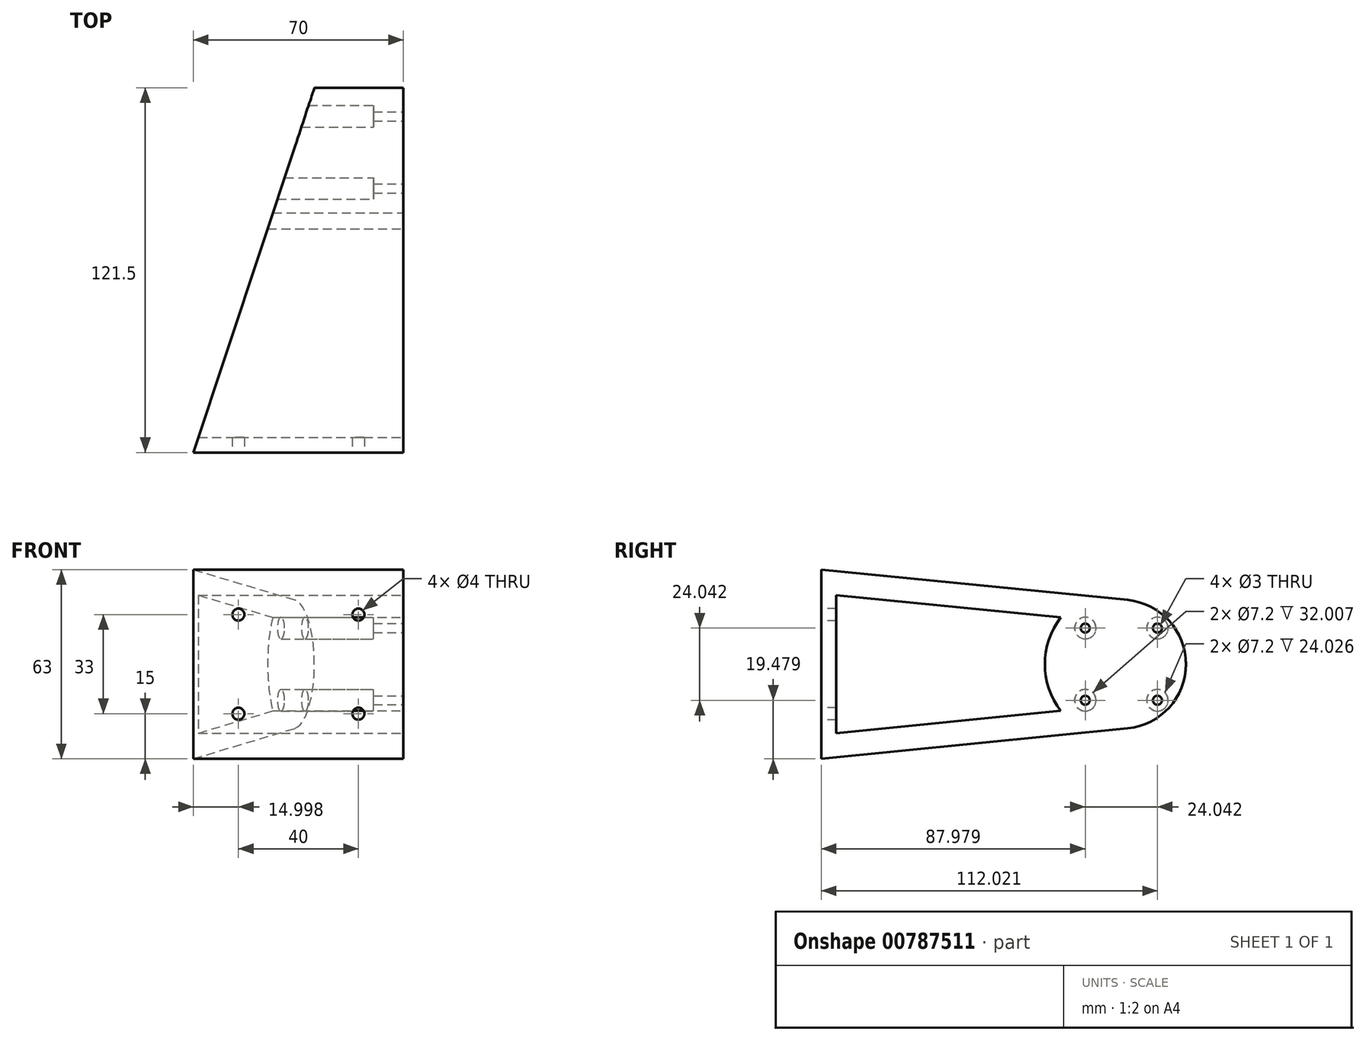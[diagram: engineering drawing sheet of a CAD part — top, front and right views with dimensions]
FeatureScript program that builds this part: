
annotation { "Feature Type Name" : "Feature", "Feature Type Description" : "" }
export const myFeature = defineFeature(function(context is Context, id is Id, definition is map)
    precondition{}
    {
        {
            var Q0;
            Q0=qCreatedBy(makeId("Top.planeOp"),FACE);
            var sketch = newSketch(context, id + "F0", { "sketchPlane" : qUnion([Q0])});
            skLineSegment(sketch, "E0", {"start": v(17.03, 72.23) * mm, "end": v(-12.97, 72.23) * mm});
            skLineSegment(sketch, "E1", {"start": v(-12.97, 72.23) * mm, "end": v(-52.97, -48.27) * mm});
            skLineSegment(sketch, "E2", {"start": v(-52.97, -48.27) * mm, "end": v(17.03, -48.27) * mm});
            skLineSegment(sketch, "E3", {"start": v(17.03, -48.27) * mm, "end": v(17.03, 72.23) * mm});
            skSolve(sketch);
        }
        {
            var Q0;
            Q0=makeQuery(id+"F0.imprint","IMPRINT",FACE,{"disambiguationData":[TD([[makeQuery(id+"F0.imprint","IMPRINT",EDGE,{"derivedFrom":sQuery(id+"F0.wireOp",EDGE,"E0")}),1.0]])]});
            extrude(context, id + "F1", {"entities" : qUnion([Q0]), "depth" : 43 * mm, "offsetDistance" : 25.4 * mm});
        }
        {
            var Q0;
            Q0=makeQuery(id+"F1.opExtrude","SWEPT_FACE",FACE,{"disambiguationData":[OSD([sQuery(id+"F0.wireOp",EDGE,"E3")])]});
            var sketch = newSketch(context, id + "F2", { "sketchPlane" : qUnion([Q0])});
            skLineSegment(sketch, "E4.bottom", {"start": v(72.23, 43) * mm, "end": v(51.73, 43) * mm});
            skLineSegment(sketch, "E4.top", {"start": v(72.23, 0) * mm, "end": v(51.73, 0) * mm});
            skLineSegment(sketch, "E4.left", {"start": v(72.23, 43) * mm, "end": v(72.23, 0) * mm});
            skLineSegment(sketch, "E4.right", {"start": v(51.73, 43) * mm, "end": v(51.73, 0) * mm, "construction": true});
            skCircle(sketch, "E5", {"center": v(51.73, 21.5) * mm, "radius": 21.5 * mm});
            skCircle(sketch, "E6", {"center": v(51.73, 21.5) * mm, "radius": 17 * mm, "construction": true});
            skCircle(sketch, "E7", {"center": v(51.73, 4.5) * mm, "radius": 1.5 * mm, "construction": true});
            skCircle(sketch, "E8.1.0", {"center": v(63.75, 9.48) * mm, "radius": 1.5 * mm});
            skCircle(sketch, "E8.2.0", {"center": v(68.73, 21.5) * mm, "radius": 1.5 * mm, "construction": true});
            skCircle(sketch, "E8.3.0", {"center": v(63.75, 33.52) * mm, "radius": 1.5 * mm});
            skCircle(sketch, "E8.4.0", {"center": v(51.73, 38.5) * mm, "radius": 1.5 * mm, "construction": true});
            skCircle(sketch, "E8.5.0", {"center": v(39.7, 33.52) * mm, "radius": 1.5 * mm});
            skCircle(sketch, "E8.6.0", {"center": v(34.73, 21.5) * mm, "radius": 1.5 * mm, "construction": true});
            skCircle(sketch, "E8.7.0", {"center": v(39.7, 9.48) * mm, "radius": 1.5 * mm});
            skLineSegment(sketch, "E9", {"start": v(-48.27, 43) * mm, "end": v(-48.27, 53) * mm});
            skLineSegment(sketch, "E10", {"start": v(-48.27, 53) * mm, "end": v(53.85, 42.9) * mm});
            skLineSegment(sketch, "E11", {"start": v(-48.27, 0) * mm, "end": v(-48.27, -10) * mm});
            skLineSegment(sketch, "E12", {"start": v(-48.27, -10) * mm, "end": v(53.85, 0.1) * mm});
            skCircle(sketch, "E13", {"center": v(51.73, 21.5) * mm, "radius": 25.5 * mm});
            skLineSegment(sketch, "E14.0", {"start": v(-48.96, -2.03) * mm, "end": v(54.65, 8.22) * mm});
            skLineSegment(sketch, "E15.0", {"start": v(-49, 45.03) * mm, "end": v(54.6, 34.78) * mm});
            skLineSegment(sketch, "E16.0", {"start": v(-43.27, 44.47) * mm, "end": v(-43.27, -1.47) * mm});
            skCircle(sketch, "E17", {"center": v(63.75, 33.52) * mm, "radius": 3.6 * mm});
            skCircle(sketch, "E18", {"center": v(63.75, 9.48) * mm, "radius": 3.6 * mm});
            skCircle(sketch, "E19", {"center": v(39.7, 33.52) * mm, "radius": 3.6 * mm});
            skCircle(sketch, "E20", {"center": v(39.7, 9.48) * mm, "radius": 3.6 * mm});
            skSolve(sketch);
        }
        {
            var Q0;
            Q0=makeQuery(id+"F2.imprint","IMPRINT",FACE,{"disambiguationData":[TD([[makeQuery(id+"F2.imprint","IMPRINT",EDGE,{"derivedFrom":sQuery(id+"F2.wireOp",EDGE,"E8.1.0")}),1.0]])]});
            var Q1;
            Q1=makeQuery(id+"F2.imprint","IMPRINT",FACE,{"disambiguationData":[TD([[makeQuery(id+"F2.imprint","IMPRINT",EDGE,{"derivedFrom":sQuery(id+"F2.wireOp",EDGE,"E8.3.0")}),1.0]])]});
            var Q2;
            Q2=makeQuery(id+"F2.imprint","IMPRINT",FACE,{"disambiguationData":[TD([[makeQuery(id+"F2.imprint","IMPRINT",EDGE,{"derivedFrom":sQuery(id+"F2.wireOp",EDGE,"E8.5.0")}),1.0]])]});
            var Q3;
            Q3=makeQuery(id+"F2.imprint","IMPRINT",FACE,{"disambiguationData":[TD([[makeQuery(id+"F2.imprint","IMPRINT",EDGE,{"derivedFrom":sQuery(id+"F2.wireOp",EDGE,"E8.7.0")}),1.0]])]});
            var Q4;
            {var subQ0=sQuery(id+"F2.wireOp",EDGE,"E4.left");var subQ1=sQuery(id+"F2.wireOp",EDGE,"E4.bottom");var subQ2=makeQuery(id+"F2.imprint","INTERSECT",VERTEX,{"derivedFrom":[subQ1,subQ0]});Q4=makeQuery(id+"F2.imprint","IMPRINT",FACE,{"disambiguationData":[TD([[makeQuery(id+"F2.imprint","IMPRINT",EDGE,{"disambiguationData":[TD([[subQ2,1.0]])],"derivedFrom":subQ1}),-1.0]])]});}
            var Q5;
            {var subQ0=sQuery(id+"F2.wireOp",EDGE,"E4.left");var subQ1=sQuery(id+"F2.wireOp",EDGE,"E4.top");var subQ2=makeQuery(id+"F2.imprint","INTERSECT",VERTEX,{"derivedFrom":[subQ1,subQ0]});Q5=makeQuery(id+"F2.imprint","IMPRINT",FACE,{"disambiguationData":[TD([[makeQuery(id+"F2.imprint","IMPRINT",EDGE,{"disambiguationData":[TD([[subQ2,1.0]])],"derivedFrom":subQ1}),1.0]])]});}
            var Q6;
            {var subQ0=sQuery(id+"F2.wireOp",EDGE,"E15.0");var subQ1=sQuery(id+"F2.wireOp",EDGE,"E13");var subQ2=makeQuery(id+"F2.imprint","INTERSECT",VERTEX,{"derivedFrom":[subQ1,subQ0]});Q6=makeQuery(id+"F2.imprint","IMPRINT",FACE,{"disambiguationData":[TD([[makeQuery(id+"F2.imprint","IMPRINT",EDGE,{"disambiguationData":[TD([[subQ2,-1.0]])],"derivedFrom":subQ1}),-1.0]])]});}
            var Q7;
            {var subQ5=sQuery(id+"F2.wireOp",EDGE,"E4.bottom");var subQ7=sQuery(id+"F2.wireOp",EDGE,"E13");var subQ9=makeQuery(id+"F2.imprint","INTERSECT",VERTEX,{"derivedFrom":[subQ5,subQ7]});Q7=makeQuery(id+"F2.imprint","IMPRINT",FACE,{"disambiguationData":[TD([[makeQuery(id+"F2.imprint","IMPRINT",EDGE,{"disambiguationData":[TD([[subQ9,1.0]])],"derivedFrom":subQ5}),-1.0]])]});}
            var Q8;
            {var subQ3=sQuery(id+"F2.wireOp",EDGE,"E4.top");var subQ7=sQuery(id+"F2.wireOp",EDGE,"E13");var subQ9=makeQuery(id+"F2.imprint","INTERSECT",VERTEX,{"derivedFrom":[subQ3,subQ7]});Q8=makeQuery(id+"F2.imprint","IMPRINT",FACE,{"disambiguationData":[TD([[makeQuery(id+"F2.imprint","IMPRINT",EDGE,{"disambiguationData":[TD([[subQ9,1.0]])],"derivedFrom":subQ3}),1.0]])]});}
            extrude(context, id + "F3", {"entities" : qUnion([Q0, Q1, Q2, Q3, Q4, Q5, Q6, Q7, Q8]), "operationType" : NewBodyOperationType.REMOVE, "oppositeDirection" : true, "depth" : 76.2 * mm, "offsetDistance" : 25.4 * mm});
        }
        {
            var Q0;
            {var subQ4=sQuery(id+"F2.wireOp",EDGE,"E14.0");var subQ6=sQuery(id+"F2.wireOp",EDGE,"E16.0");var subQ8=makeQuery(id+"F2.imprint","INTERSECT",VERTEX,{"derivedFrom":[subQ4,subQ6]});Q0=makeQuery(id+"F2.imprint","IMPRINT",FACE,{"disambiguationData":[TD([[makeQuery(id+"F2.imprint","IMPRINT",EDGE,{"disambiguationData":[TD([[subQ8,1.0]])],"derivedFrom":subQ4}),1.0]])]});}
            var Q1;
            {var subQ1=sQuery(id+"F2.wireOp",EDGE,"E12");var subQ5=sQuery(id+"F2.wireOp",EDGE,"E11");var subQ6=makeQuery(id+"F2.imprint","INTERSECT",VERTEX,{"derivedFrom":[subQ5,subQ1]});Q1=makeQuery(id+"F2.imprint","IMPRINT",FACE,{"disambiguationData":[TD([[makeQuery(id+"F2.imprint","IMPRINT",EDGE,{"disambiguationData":[TD([[subQ6,1.0]])],"derivedFrom":subQ5}),1.0]])]});}
            var Q2;
            {var subQ4=sQuery(id+"F2.wireOp",EDGE,"E15.0");var subQ6=sQuery(id+"F2.wireOp",EDGE,"E16.0");var subQ7=makeQuery(id+"F2.imprint","INTERSECT",VERTEX,{"derivedFrom":[subQ4,subQ6]});Q2=makeQuery(id+"F2.imprint","IMPRINT",FACE,{"disambiguationData":[TD([[makeQuery(id+"F2.imprint","IMPRINT",EDGE,{"disambiguationData":[TD([[subQ7,1.0]])],"derivedFrom":subQ4}),-1.0]])]});}
            var Q3;
            {var subQ1=sQuery(id+"F2.wireOp",EDGE,"E10");var subQ7=sQuery(id+"F2.wireOp",EDGE,"E9");var subQ9=makeQuery(id+"F2.imprint","INTERSECT",VERTEX,{"derivedFrom":[subQ7,subQ1]});Q3=makeQuery(id+"F2.imprint","IMPRINT",FACE,{"disambiguationData":[TD([[makeQuery(id+"F2.imprint","IMPRINT",EDGE,{"disambiguationData":[TD([[subQ9,1.0]])],"derivedFrom":subQ7}),-1.0]])]});}
            var Q4;
            {var subQ3=sQuery(id+"F2.wireOp",EDGE,"E10");var subQ5=sQuery(id+"F2.wireOp",EDGE,"E13");var subQ6=makeQuery(id+"F2.imprint","INTERSECT",VERTEX,{"derivedFrom":[subQ3,subQ5]});Q4=makeQuery(id+"F2.imprint","IMPRINT",FACE,{"disambiguationData":[TD([[makeQuery(id+"F2.imprint","IMPRINT",EDGE,{"disambiguationData":[TD([[subQ6,-1.0]])],"derivedFrom":subQ3}),-1.0]])]});}
            var Q5;
            {var subQ3=sQuery(id+"F2.wireOp",EDGE,"E12");var subQ5=sQuery(id+"F2.wireOp",EDGE,"E13");var subQ6=makeQuery(id+"F2.imprint","INTERSECT",VERTEX,{"derivedFrom":[subQ3,subQ5]});Q5=makeQuery(id+"F2.imprint","IMPRINT",FACE,{"disambiguationData":[TD([[makeQuery(id+"F2.imprint","IMPRINT",EDGE,{"disambiguationData":[TD([[subQ6,-1.0]])],"derivedFrom":subQ3}),1.0]])]});}
            var Q6;
            {var subQ0=sQuery(id+"F2.wireOp",EDGE,"E5");var subQ1=sQuery(id+"F2.wireOp",EDGE,"E4.left");var subQ2=makeQuery(id+"F2.imprint","INTERSECT",VERTEX,{"disambiguationData":[OD(0.0)],"derivedFrom":[subQ1,subQ0]});Q6=makeQuery(id+"F2.imprint","IMPRINT",FACE,{"disambiguationData":[TD([[makeQuery(id+"F2.imprint","IMPRINT",EDGE,{"disambiguationData":[TD([[subQ2,-1.0]])],"derivedFrom":subQ1}),1.0]])]});}
            var Q7;
            {var subQ3=sQuery(id+"F0.wireOp",EDGE,"E1");Q7=makeQuery(id+"F3.boolean.opBoolean","SPLIT",FACE,{"disambiguationData":[TD([makeQuery(id+"F3.opExtrude","SWEPT_FACE",FACE,{"disambiguationData":[OSD([sQuery(id+"F2.wireOp",EDGE,"E8.1.0")])]})])],"derivedFrom":makeQuery(id+"F1.opExtrude","SWEPT_FACE",FACE,{"disambiguationData":[OSD([subQ3])]})});}
            extrude(context, id + "F4", {"entities" : qUnion([Q0, Q1, Q2, Q3, Q4, Q5, Q6]), "operationType" : NewBodyOperationType.ADD, "endBound" : BoundingType.UP_TO_SURFACE, "oppositeDirection" : true, "depth" : 25.4 * mm, "endBoundEntityFace" : qUnion([Q7]), "offsetDistance" : 25.4 * mm});
        }
        {
            var Q0;
            Q0=makeQuery(id+"F4.boolean.opBoolean","MERGE",FACE,{"derivedFrom":[makeQuery(id+"F1.opExtrude","SWEPT_FACE",FACE,{"disambiguationData":[OSD([sQuery(id+"F0.wireOp",EDGE,"E2")])]}),makeQuery(id+"F4.opExtrude","SWEPT_FACE",FACE,{"disambiguationData":[OSD([sQuery(id+"F2.wireOp",EDGE,"E9")])]}),makeQuery(id+"F4.opExtrude","SWEPT_FACE",FACE,{"disambiguationData":[OSD([sQuery(id+"F2.wireOp",EDGE,"E11")])]})]});
            var sketch = newSketch(context, id + "F5", { "sketchPlane" : qUnion([Q0])});
            skLineSegment(sketch, "E21.bottom", {"start": v(-52.97, 53) * mm, "end": v(17.03, 53) * mm});
            skLineSegment(sketch, "E21.top", {"start": v(-52.97, -10) * mm, "end": v(17.03, -10) * mm});
            skLineSegment(sketch, "E21.left", {"start": v(-52.97, 53) * mm, "end": v(-52.97, -10) * mm});
            skLineSegment(sketch, "E21.right", {"start": v(17.03, 53) * mm, "end": v(17.03, -10) * mm});
            skLineSegment(sketch, "E22.0", {"start": v(-37.97, 38) * mm, "end": v(2.03, 38) * mm, "construction": true});
            skLineSegment(sketch, "E22.1", {"start": v(-37.97, 38) * mm, "end": v(-37.97, 5) * mm, "construction": true});
            skLineSegment(sketch, "E22.2", {"start": v(-37.97, 5) * mm, "end": v(2.03, 5) * mm, "construction": true});
            skLineSegment(sketch, "E22.3", {"start": v(2.03, 38) * mm, "end": v(2.03, 5) * mm, "construction": true});
            skCircle(sketch, "E23", {"center": v(2.03, 38) * mm, "radius": 2 * mm});
            skCircle(sketch, "E24", {"center": v(2.03, 5) * mm, "radius": 2 * mm});
            skCircle(sketch, "E25", {"center": v(-37.97, 5) * mm, "radius": 2 * mm});
            skCircle(sketch, "E26", {"center": v(-37.97, 38) * mm, "radius": 2 * mm});
            skSolve(sketch);
        }
        {
            var Q0;
            Q0=makeQuery(id+"F5.imprint","IMPRINT",FACE,{"disambiguationData":[TD([[makeQuery(id+"F5.imprint","IMPRINT",EDGE,{"derivedFrom":sQuery(id+"F5.wireOp",EDGE,"E24")}),1.0]])]});
            var Q1;
            Q1=makeQuery(id+"F5.imprint","IMPRINT",FACE,{"disambiguationData":[TD([[makeQuery(id+"F5.imprint","IMPRINT",EDGE,{"derivedFrom":sQuery(id+"F5.wireOp",EDGE,"E23")}),1.0]])]});
            var Q2;
            Q2=makeQuery(id+"F5.imprint","IMPRINT",FACE,{"disambiguationData":[TD([[makeQuery(id+"F5.imprint","IMPRINT",EDGE,{"derivedFrom":sQuery(id+"F5.wireOp",EDGE,"E26")}),1.0]])]});
            var Q3;
            Q3=makeQuery(id+"F5.imprint","IMPRINT",FACE,{"disambiguationData":[TD([[makeQuery(id+"F5.imprint","IMPRINT",EDGE,{"derivedFrom":sQuery(id+"F5.wireOp",EDGE,"E25")}),1.0]])]});
            extrude(context, id + "F6", {"entities" : qUnion([Q0, Q1, Q2, Q3]), "operationType" : NewBodyOperationType.REMOVE, "oppositeDirection" : true, "depth" : 5 * mm, "offsetDistance" : 25.4 * mm});
        }
        {
            var Q0;
            Q0=makeQuery(id+"F2.imprint","IMPRINT",FACE,{"disambiguationData":[TD([[makeQuery(id+"F2.imprint","IMPRINT",EDGE,{"derivedFrom":sQuery(id+"F2.wireOp",EDGE,"E8.3.0")}),-1.0]])]});
            var Q1;
            Q1=makeQuery(id+"F2.imprint","IMPRINT",FACE,{"disambiguationData":[TD([[makeQuery(id+"F2.imprint","IMPRINT",EDGE,{"derivedFrom":sQuery(id+"F2.wireOp",EDGE,"E8.5.0")}),-1.0]])]});
            var Q2;
            {var subQ0=sQuery(id+"F2.wireOp",EDGE,"E19");var subQ1=sQuery(id+"F2.wireOp",EDGE,"E15.0");var subQ2=makeQuery(id+"F2.imprint","INTERSECT",VERTEX,{"disambiguationData":[OD(0.0)],"derivedFrom":[subQ1,subQ0]});Q2=makeQuery(id+"F2.imprint","IMPRINT",FACE,{"disambiguationData":[TD([[makeQuery(id+"F2.imprint","IMPRINT",EDGE,{"disambiguationData":[TD([[subQ2,-1.0]])],"derivedFrom":subQ1}),1.0]])]});}
            var Q3;
            {var subQ0=sQuery(id+"F2.wireOp",EDGE,"E20");var subQ1=sQuery(id+"F2.wireOp",EDGE,"E14.0");var subQ2=makeQuery(id+"F2.imprint","INTERSECT",VERTEX,{"disambiguationData":[OD(0.0)],"derivedFrom":[subQ1,subQ0]});Q3=makeQuery(id+"F2.imprint","IMPRINT",FACE,{"disambiguationData":[TD([[makeQuery(id+"F2.imprint","IMPRINT",EDGE,{"disambiguationData":[TD([[subQ2,-1.0]])],"derivedFrom":subQ1}),-1.0]])]});}
            var Q4;
            Q4=makeQuery(id+"F2.imprint","IMPRINT",FACE,{"disambiguationData":[TD([[makeQuery(id+"F2.imprint","IMPRINT",EDGE,{"derivedFrom":sQuery(id+"F2.wireOp",EDGE,"E8.7.0")}),-1.0]])]});
            var Q5;
            Q5=makeQuery(id+"F2.imprint","IMPRINT",FACE,{"disambiguationData":[TD([[makeQuery(id+"F2.imprint","IMPRINT",EDGE,{"derivedFrom":sQuery(id+"F2.wireOp",EDGE,"E8.1.0")}),-1.0]])]});
            extrude(context, id + "F7", {"entities" : qUnion([Q0, Q1, Q2, Q3, Q4, Q5]), "operationType" : NewBodyOperationType.REMOVE, "oppositeDirection" : true, "depth" : 50 * mm, "offsetDistance" : 25.4 * mm, "hasSecondDirection" : true, "secondDirectionOppositeDirection" : true, "secondDirectionDepth" : 10 * mm});
        }
    });
